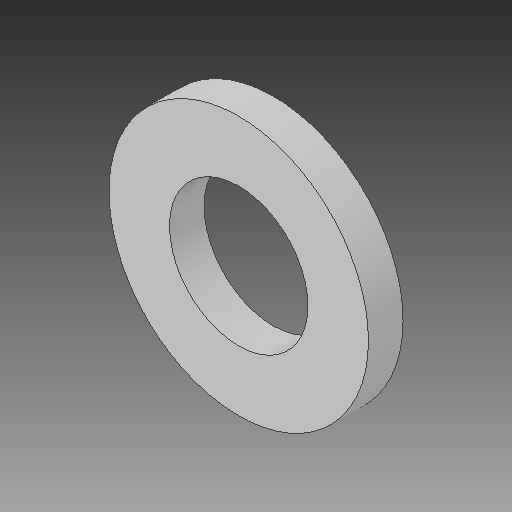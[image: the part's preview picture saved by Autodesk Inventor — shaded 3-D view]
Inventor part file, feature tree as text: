
AUTODESK INVENTOR PART (.ipt)
format: ipt  version: 2017 (Build 210142000, 142)  size: 92,672 bytes
history: native  units: mm
features: other x3, sketch x1
ambient origin geometry x8: Origin, YZ Plane, XZ Plane, XY Plane, X Axis, Y Axis, Z Axis, Center Point
bodies: Solid1 (feature_tree)
feature tree (4):
  other  "M3 Washer.ipt"
  other  "Solid1::M3 Washer.ipt"
  other  "TaggingFeature1"
  sketch  "Sketch1"  dims[d0=10.0mm]
